# Revit family: Urinal-American_Standard-Greenbrook-651X001EC_Series
name_source: partatom
category: Plumbing Fixtures
revit_build: Autodesk Revit 2014 (Build: 20130308_1515(x64)
units: mm (PartAtom-declared; Revit-internal decimal feet)

## types (2) — shared parameters
ADA Compliant = Yes
Assembly Code = D2010210
CW Connection = Yes
CWFU = 5
Cold Water Connection Diameter = 3/4"
Cold Water Connection Height = 11 1/2"
Cold Water Connection Radius = 3/8"
Cold Water Connection Width = 4 1/4"
Default Elevation = 17"
Description = Greenbrook Urinal
Finish = Vitreous China-American Standard-020-White
Flow Rate = 0.125 gpf (0.47 Lpf) to 0.5 gpf (1.9 Lpf)
HW Connection = No
Height = 27 1/2"
Installation Type = Wall Mounted
Length = 15"
Manufacturer = American Standard
Material = Vitreous China-American Standard-020-White
Price = Prices may vary. Please consult Manufacturer Representative for most up-to-date price list.
URL = https://www.americanstandard-us.com
Vent Connection = No
WFU = 5
Waste Connection = Yes
Waste Connection Diameter = 2"
Waste Connection Height = 4 3/4"
Waste Connection Radius = 1"
Width = 16 1/8"
zero-valued in all types: HWFU

## per-type parameters (varying)
| type | Back Spud | Top Spud |
| 6516001EC.020 | No | Yes |
| 6517001EC.020 | Yes | No |

note: column(s) folded — value = type name in every type: Model

## geometry (parser evidence)
native form markers: Sweep x1
no freeform markers — native parametric forms only
